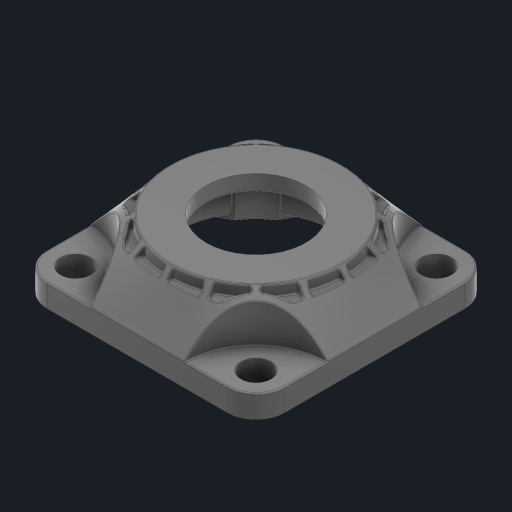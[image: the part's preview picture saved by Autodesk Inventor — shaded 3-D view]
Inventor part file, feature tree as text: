
AUTODESK INVENTOR PART (.ipt)
format: ipt  version: 2023 (Build 270158030, 158C)  size: 2,892,288 bytes
history: native  units: in
note: dims shown in document units (in); Inventor stores cm internally (conversion verified against a paired STEP export)
features: fillet x1
ambient origin geometry x8: Origin, YZ Plane, XZ Plane, XY Plane, X Axis, Y Axis, Z Axis, Center Point
bodies: Solid1 (feature_tree)
feature tree (1):
  fillet  "Fillet52"  [1 undecoded]
note: 1 required parameter value undecoded (feature->parameter linkage not recoverable at this tier; creation-order binding heuristic only, values carry confidence <= 0.55)
